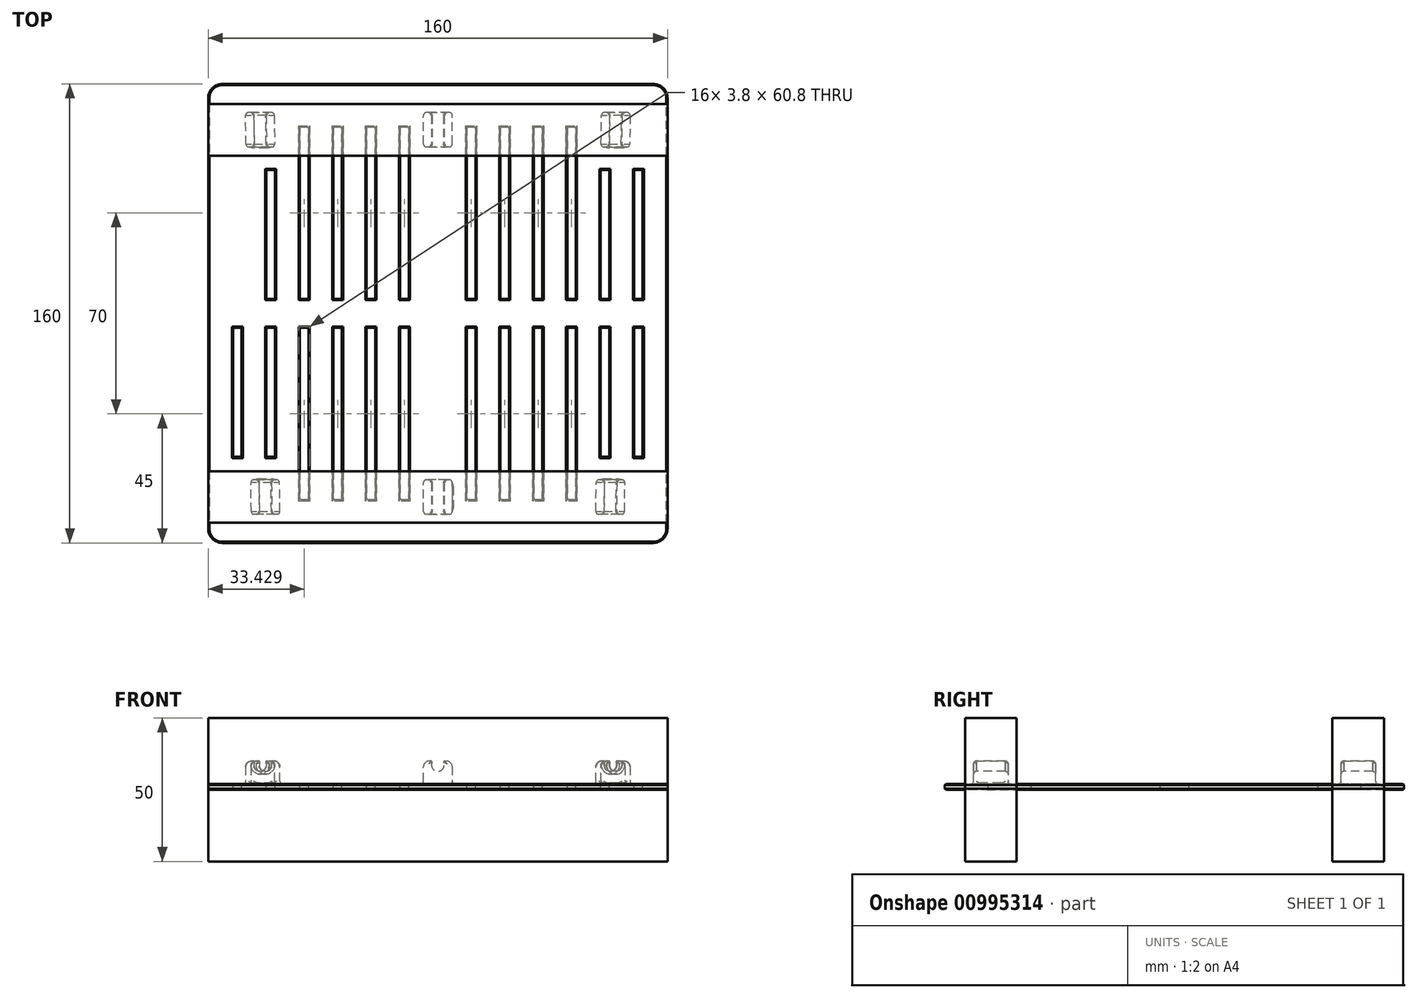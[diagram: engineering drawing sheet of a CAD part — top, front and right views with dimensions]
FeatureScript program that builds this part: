
annotation { "Feature Type Name" : "Feature", "Feature Type Description" : "" }
export const myFeature = defineFeature(function(context is Context, id is Id, definition is map)
    precondition{}
    {
        {
            var Q0;
            Q0=qCreatedBy(makeId("Front.planeOp"),FACE);
            cPlane(context, id + "F0", {"entities" : qUnion([Q0]), "cplaneType" : CPlaneType.OFFSET, "offset" : 70 * mm, "width" : 150 * mm, "height" : 150 * mm});
        }
        {
            var Q0;
            Q0=qCreatedBy(makeId("Front.planeOp"),FACE);
            cPlane(context, id + "F1", {"entities" : qUnion([Q0]), "cplaneType" : CPlaneType.OFFSET, "offset" : 70 * mm, "oppositeDirection" : true, "width" : 150 * mm, "height" : 150 * mm});
        }
        {
            var Q0;
            Q0=qCreatedBy(makeId("Top.planeOp"),FACE);
            cPlane(context, id + "F2", {"entities" : qUnion([Q0]), "cplaneType" : CPlaneType.OFFSET, "offset" : 25 * mm, "width" : 150 * mm, "height" : 150 * mm});
        }
        {
            var Q0;
            Q0=qCreatedBy(makeId("Top.planeOp"),FACE);
            var sketch = newSketch(context, id + "F3", { "sketchPlane" : qUnion([Q0])});
            skLineSegment(sketch, "E0.bottom", {"start": v(-75, 80) * mm, "end": v(75, 80) * mm});
            skLineSegment(sketch, "E0.top", {"start": v(-75, -80) * mm, "end": v(75, -80) * mm});
            skLineSegment(sketch, "E0.left", {"start": v(-80, 75) * mm, "end": v(-80, -75) * mm});
            skLineSegment(sketch, "E0.right", {"start": v(80, 75) * mm, "end": v(80, -75) * mm});
            skLineSegment(sketch, "E1", {"start": v(-80, 80) * mm, "end": v(80, -80) * mm, "construction": true});
            skPoint(sketch, "E2.visualSharp", {"position": v(-80, 80) * mm});
            skArc(sketch, "E2.filletArc", {"start": v(-75, 80) * mm, "mid": v(-78.54, 78.54) * mm, "end": v(-80, 75) * mm});
            skPoint(sketch, "E3.visualSharp", {"position": v(80, 80) * mm});
            skArc(sketch, "E3.filletArc", {"start": v(80, 75) * mm, "mid": v(78.54, 78.54) * mm, "end": v(75, 80) * mm});
            skPoint(sketch, "E4.visualSharp", {"position": v(80, -80) * mm});
            skArc(sketch, "E4.filletArc", {"start": v(75, -80) * mm, "mid": v(78.54, -78.54) * mm, "end": v(80, -75) * mm});
            skPoint(sketch, "E5.visualSharp", {"position": v(-80, -80) * mm});
            skArc(sketch, "E5.filletArc", {"start": v(-80, -75) * mm, "mid": v(-78.54, -78.54) * mm, "end": v(-75, -80) * mm});
            skSolve(sketch);
        }
        {
            var Q0;
            Q0 = qSketchRegion(id + "F3", true);
            extrude(context, id + "F4", {"entities" : qUnion([Q0]), "depth" : 2 * mm, "offsetDistance" : 25 * mm});
        }
        {
            var Q0;
            Q0=qCreatedBy(makeId("Right.planeOp"),FACE);
            var sketch = newSketch(context, id + "F5", { "sketchPlane" : qUnion([Q0])});
            skLineSegment(sketch, "E6.0", {"start": v(75, 2) * mm, "end": v(-75, 2) * mm, "construction": true});
            skLineSegment(sketch, "E7", {"start": v(0, 2) * mm, "end": v(0, -33.18) * mm, "construction": true});
            skLineSegment(sketch, "E8", {"start": v(0, 2) * mm, "end": v(58, 2) * mm});
            skLineSegment(sketch, "E9", {"start": v(58, 2) * mm, "end": v(58, 12) * mm});
            skLineSegment(sketch, "E10", {"start": v(58, 12) * mm, "end": v(-58, 12) * mm});
            skLineSegment(sketch, "E11", {"start": v(-58, 12) * mm, "end": v(-58, 2) * mm});
            skLineSegment(sketch, "E12", {"start": v(-58, 2) * mm, "end": v(0, 2) * mm});
            skSolve(sketch);
        }
        {
            var Q0;
            Q0=qCreatedBy(id+"F0.planeOp",FACE);
            var sketch = newSketch(context, id + "F6", { "sketchPlane" : qUnion([Q0])});
            skLineSegment(sketch, "E13.0", {"start": v(-75, 2) * mm, "end": v(75, 2) * mm, "construction": true});
            skLineSegment(sketch, "E14.bottom", {"start": v(55, 2) * mm, "end": v(65, 2) * mm});
            skLineSegment(sketch, "E14.top", {"start": v(55, 10) * mm, "end": v(65, 10) * mm, "construction": true});
            skLineSegment(sketch, "E14.left", {"start": v(55, 2) * mm, "end": v(55, 10) * mm});
            skLineSegment(sketch, "E14.right", {"start": v(65, 2) * mm, "end": v(65, 10) * mm});
            skLineSegment(sketch, "E15", {"start": v(0, 2) * mm, "end": v(0, 47.73) * mm, "construction": true});
            skArc(sketch, "E16", {"start": v(58.3, 10) * mm, "mid": v(60, 6.4) * mm, "end": v(61.7, 10) * mm});
            skLineSegment(sketch, "E17", {"start": v(60, 10) * mm, "end": v(60, 8.6) * mm, "construction": true});
            skLineSegment(sketch, "E18", {"start": v(55, 10) * mm, "end": v(58.3, 10) * mm});
            skLineSegment(sketch, "E19", {"start": v(65, 10) * mm, "end": v(61.7, 10) * mm});
            skLineSegment(sketch, "E20.MirrorCS", {"start": v(-55, 10) * mm, "end": v(-65, 10) * mm, "construction": true});
            skLineSegment(sketch, "E21.MirrorCS", {"start": v(-60, 10) * mm, "end": v(-60, 8.6) * mm, "construction": true});
            skLineSegment(sketch, "E22.MirrorCS", {"start": v(-55, 10) * mm, "end": v(-58.3, 10) * mm});
            skLineSegment(sketch, "E23.MirrorCS", {"start": v(-65, 10) * mm, "end": v(-61.7, 10) * mm});
            skLineSegment(sketch, "E24.MirrorCS", {"start": v(-55, 2) * mm, "end": v(-65, 2) * mm});
            skLineSegment(sketch, "E25.MirrorCS", {"start": v(-55, 2) * mm, "end": v(-55, 10) * mm});
            skLineSegment(sketch, "E26.MirrorCS", {"start": v(-65, 2) * mm, "end": v(-65, 10) * mm});
            skArc(sketch, "E27.MirrorCS", {"start": v(-58.3, 10) * mm, "mid": v(-60, 6.4) * mm, "end": v(-61.7, 10) * mm});
            skLineSegment(sketch, "E28", {"start": v(30, 2) * mm, "end": v(30, 33.9) * mm, "construction": true});
            skLineSegment(sketch, "E29", {"start": v(60, 8.6) * mm, "end": v(30, 8.6) * mm, "construction": true});
            skLineSegment(sketch, "E30", {"start": v(30, 8.6) * mm, "end": v(0, 8.6) * mm, "construction": true});
            skLineSegment(sketch, "E31.MirrorCS", {"start": v(-5, 10) * mm, "end": v(-1.7, 10) * mm});
            skLineSegment(sketch, "E32.MirrorCS", {"start": v(5, 10) * mm, "end": v(1.7, 10) * mm});
            skLineSegment(sketch, "E33.MirrorCS", {"start": v(-5, 2) * mm, "end": v(-5, 10) * mm});
            skLineSegment(sketch, "E34.MirrorCS", {"start": v(5, 10) * mm, "end": v(-5, 10) * mm, "construction": true});
            skLineSegment(sketch, "E35.MirrorCS", {"start": v(0, 10) * mm, "end": v(0, 8.6) * mm, "construction": true});
            skLineSegment(sketch, "E36.MirrorCS", {"start": v(5, 2) * mm, "end": v(-5, 2) * mm});
            skLineSegment(sketch, "E37.MirrorCS", {"start": v(5, 2) * mm, "end": v(5, 10) * mm});
            skArc(sketch, "E38.MirrorCS", {"start": v(1.7, 10) * mm, "mid": v(0, 6.4) * mm, "end": v(-1.7, 10) * mm});
            skSolve(sketch);
        }
        {
            var Q0;
            Q0=qCreatedBy(id+"F1.planeOp",FACE);
            var sketch = newSketch(context, id + "F7", { "sketchPlane" : qUnion([Q0])});
            skLineSegment(sketch, "E39.bottom", {"start": v(57, 2) * mm, "end": v(67, 2) * mm});
            skLineSegment(sketch, "E39.top", {"start": v(57, 10) * mm, "end": v(67, 10) * mm, "construction": true});
            skLineSegment(sketch, "E39.left", {"start": v(57, 2) * mm, "end": v(57, 10) * mm});
            skLineSegment(sketch, "E39.right", {"start": v(67, 2) * mm, "end": v(67, 10) * mm});
            skArc(sketch, "E40", {"start": v(60.3, 10) * mm, "mid": v(62, 6.4) * mm, "end": v(63.7, 10) * mm});
            skLineSegment(sketch, "E41", {"start": v(62, 10) * mm, "end": v(62, 8.6) * mm, "construction": true});
            skLineSegment(sketch, "E42", {"start": v(57, 10) * mm, "end": v(60.3, 10) * mm});
            skLineSegment(sketch, "E43", {"start": v(67, 10) * mm, "end": v(63.7, 10) * mm});
            skLineSegment(sketch, "E44.0", {"start": v(-75, 2) * mm, "end": v(75, 2) * mm, "construction": true});
            skLineSegment(sketch, "E45", {"start": v(0, 2) * mm, "end": v(0, 63.92) * mm, "construction": true});
            skPoint(sketch, "E45.endSnap0", {"position": v(0, 2) * mm});
            skLineSegment(sketch, "E46.MirrorCS", {"start": v(-67, 10) * mm, "end": v(-63.7, 10) * mm});
            skLineSegment(sketch, "E47.MirrorCS", {"start": v(-57, 10) * mm, "end": v(-60.3, 10) * mm});
            skLineSegment(sketch, "E48.MirrorCS", {"start": v(-57, 10) * mm, "end": v(-67, 10) * mm, "construction": true});
            skLineSegment(sketch, "E49.MirrorCS", {"start": v(-62, 10) * mm, "end": v(-62, 8.6) * mm, "construction": true});
            skLineSegment(sketch, "E50.MirrorCS", {"start": v(-67, 2) * mm, "end": v(-67, 10) * mm});
            skLineSegment(sketch, "E51.MirrorCS", {"start": v(-57, 2) * mm, "end": v(-67, 2) * mm});
            skArc(sketch, "E52.MirrorCS", {"start": v(-60.3, 10) * mm, "mid": v(-62, 6.4) * mm, "end": v(-63.7, 10) * mm});
            skLineSegment(sketch, "E53.MirrorCS", {"start": v(-57, 2) * mm, "end": v(-57, 10) * mm});
            skLineSegment(sketch, "E54", {"start": v(31, 2) * mm, "end": v(31, 36.18) * mm, "construction": true});
            skLineSegment(sketch, "E55", {"start": v(62, 8.6) * mm, "end": v(31, 8.6) * mm, "construction": true});
            skLineSegment(sketch, "E56", {"start": v(31, 8.6) * mm, "end": v(0, 8.6) * mm, "construction": true});
            skLineSegment(sketch, "E57.MirrorCS", {"start": v(5, 10) * mm, "end": v(1.7, 10) * mm});
            skLineSegment(sketch, "E58.MirrorCS", {"start": v(5, 10) * mm, "end": v(-5, 10) * mm, "construction": true});
            skLineSegment(sketch, "E59.MirrorCS", {"start": v(0, 10) * mm, "end": v(0, 8.6) * mm, "construction": true});
            skLineSegment(sketch, "E60.MirrorCS", {"start": v(-5, 10) * mm, "end": v(-1.7, 10) * mm});
            skArc(sketch, "E61.MirrorCS", {"start": v(1.7, 10) * mm, "mid": v(0, 6.4) * mm, "end": v(-1.7, 10) * mm});
            skLineSegment(sketch, "E62.MirrorCS", {"start": v(5, 2) * mm, "end": v(5, 10) * mm});
            skLineSegment(sketch, "E63.MirrorCS", {"start": v(5, 2) * mm, "end": v(-5, 2) * mm});
            skLineSegment(sketch, "E64.MirrorCS", {"start": v(-5, 2) * mm, "end": v(-5, 10) * mm});
            skSolve(sketch);
        }
        {
            var Q1;
            Q1=makeQuery(id+"F6.imprint","IMPRINT",FACE,{"disambiguationData":[TD([[makeQuery(id+"F6.imprint","IMPRINT",EDGE,{"derivedFrom":sQuery(id+"F6.wireOp",EDGE,"E14.bottom")}),1.0]])]});
            var Q2;
            Q2=makeQuery(id+"F7.imprint","IMPRINT",FACE,{"disambiguationData":[TD([[makeQuery(id+"F7.imprint","IMPRINT",EDGE,{"derivedFrom":sQuery(id+"F7.wireOp",EDGE,"E39.bottom")}),1.0]])]});
            loft(context, id + "F8", {"operationType" : NewBodyOperationType.ADD, "sheetProfilesArray" : [{ "sheetProfileEntities" : qUnion([Q1]) }, { "sheetProfileEntities" : qUnion([Q2]) }]});
        }
        {
            var Q1;
            Q1=makeQuery(id+"F6.imprint","IMPRINT",FACE,{"disambiguationData":[TD([[makeQuery(id+"F6.imprint","IMPRINT",EDGE,{"derivedFrom":sQuery(id+"F6.wireOp",EDGE,"E22.MirrorCS")}),1.0]])]});
            var Q2;
            Q2=makeQuery(id+"F7.imprint","IMPRINT",FACE,{"disambiguationData":[TD([[makeQuery(id+"F7.imprint","IMPRINT",EDGE,{"derivedFrom":sQuery(id+"F7.wireOp",EDGE,"E47.MirrorCS")}),1.0]])]});
            loft(context, id + "F9", {"operationType" : NewBodyOperationType.ADD, "sheetProfilesArray" : [{ "sheetProfileEntities" : qUnion([Q1]) }, { "sheetProfileEntities" : qUnion([Q2]) }]});
        }
        {
            var Q1;
            Q1=makeQuery(id+"F6.imprint","IMPRINT",FACE,{"disambiguationData":[TD([[makeQuery(id+"F6.imprint","IMPRINT",EDGE,{"derivedFrom":sQuery(id+"F6.wireOp",EDGE,"E31.MirrorCS")}),-1.0]])]});
            var Q2;
            Q2=makeQuery(id+"F7.imprint","IMPRINT",FACE,{"disambiguationData":[TD([[makeQuery(id+"F7.imprint","IMPRINT",EDGE,{"derivedFrom":sQuery(id+"F7.wireOp",EDGE,"E57.MirrorCS")}),1.0]])]});
            loft(context, id + "F10", {"operationType" : NewBodyOperationType.ADD, "sheetProfilesArray" : [{ "sheetProfileEntities" : qUnion([Q1]) }, { "sheetProfileEntities" : qUnion([Q2]) }]});
        }
        {
            var Q0;
            Q0 = qSketchRegion(id + "F5", true);
            extrude(context, id + "F11", {"entities" : qUnion([Q0]), "operationType" : NewBodyOperationType.REMOVE, "endBound" : BoundingType.SYMMETRIC, "depth" : 140 * mm, "offsetDistance" : 25 * mm});
        }
        {
            var Q0;
            Q0=makeQuery(id+"F8.opLoft","SWEPT_EDGE",EDGE,{"disambiguationData":[OSD([sQuery(id+"F6.wireOp",EDGE,"E14.left"),sQuery(id+"F6.wireOp",EDGE,"E18"),sQuery(id+"F7.wireOp",EDGE,"E39.left"),sQuery(id+"F7.wireOp",EDGE,"E42")])]});
            var Q1;
            Q1=makeQuery(id+"F8.opLoft","SWEPT_EDGE",EDGE,{"disambiguationData":[OSD([sQuery(id+"F6.wireOp",EDGE,"E14.right"),sQuery(id+"F6.wireOp",EDGE,"E19"),sQuery(id+"F7.wireOp",EDGE,"E39.right"),sQuery(id+"F7.wireOp",EDGE,"E43")])]});
            var Q2;
            Q2=makeQuery(id+"F9.opLoft","SWEPT_EDGE",EDGE,{"disambiguationData":[OSD([sQuery(id+"F6.wireOp",EDGE,"E23.MirrorCS"),sQuery(id+"F6.wireOp",EDGE,"E26.MirrorCS"),sQuery(id+"F7.wireOp",EDGE,"E46.MirrorCS"),sQuery(id+"F7.wireOp",EDGE,"E50.MirrorCS")])]});
            var Q3;
            Q3=makeQuery(id+"F9.opLoft","SWEPT_EDGE",EDGE,{"disambiguationData":[OSD([sQuery(id+"F6.wireOp",EDGE,"E22.MirrorCS"),sQuery(id+"F6.wireOp",EDGE,"E25.MirrorCS"),sQuery(id+"F7.wireOp",EDGE,"E47.MirrorCS"),sQuery(id+"F7.wireOp",EDGE,"E53.MirrorCS")])]});
            var Q4;
            {var subQ0=sQuery(id+"F7.wireOp",EDGE,"E64.MirrorCS");var subQ1=sQuery(id+"F7.wireOp",EDGE,"E60.MirrorCS");var subQ3=sQuery(id+"F6.wireOp",EDGE,"E33.MirrorCS");var subQ4=sQuery(id+"F6.wireOp",EDGE,"E31.MirrorCS");Q4=makeQuery(id+"F11.boolean.opBoolean","SPLIT",EDGE,{"disambiguationData":[TD([makeQuery(id+"F11.opExtrude","SWEPT_FACE",FACE,{"disambiguationData":[OSD([sQuery(id+"F5.wireOp",EDGE,"E11")])]})])],"derivedFrom":makeQuery(id+"F10.opLoft","SWEPT_EDGE",EDGE,{"disambiguationData":[OSD([subQ4,subQ3,subQ1,subQ0])]})});}
            var Q5;
            {var subQ0=sQuery(id+"F7.wireOp",EDGE,"E62.MirrorCS");var subQ1=sQuery(id+"F7.wireOp",EDGE,"E57.MirrorCS");var subQ3=sQuery(id+"F6.wireOp",EDGE,"E37.MirrorCS");var subQ4=sQuery(id+"F6.wireOp",EDGE,"E32.MirrorCS");Q5=makeQuery(id+"F11.boolean.opBoolean","SPLIT",EDGE,{"disambiguationData":[TD([makeQuery(id+"F11.opExtrude","SWEPT_FACE",FACE,{"disambiguationData":[OSD([sQuery(id+"F5.wireOp",EDGE,"E11")])]})])],"derivedFrom":makeQuery(id+"F10.opLoft","SWEPT_EDGE",EDGE,{"disambiguationData":[OSD([subQ4,subQ3,subQ1,subQ0])]})});}
            var Q6;
            {var subQ0=sQuery(id+"F7.wireOp",EDGE,"E64.MirrorCS");var subQ2=sQuery(id+"F7.wireOp",EDGE,"E60.MirrorCS");var subQ3=sQuery(id+"F6.wireOp",EDGE,"E33.MirrorCS");var subQ4=sQuery(id+"F6.wireOp",EDGE,"E31.MirrorCS");Q6=makeQuery(id+"F11.boolean.opBoolean","SPLIT",EDGE,{"disambiguationData":[TD([makeQuery(id+"F11.opExtrude","SWEPT_FACE",FACE,{"disambiguationData":[OSD([sQuery(id+"F5.wireOp",EDGE,"E9")])]})])],"derivedFrom":makeQuery(id+"F10.opLoft","SWEPT_EDGE",EDGE,{"disambiguationData":[OSD([subQ4,subQ3,subQ2,subQ0])]})});}
            var Q7;
            {var subQ0=sQuery(id+"F7.wireOp",EDGE,"E62.MirrorCS");var subQ2=sQuery(id+"F7.wireOp",EDGE,"E57.MirrorCS");var subQ3=sQuery(id+"F6.wireOp",EDGE,"E37.MirrorCS");var subQ4=sQuery(id+"F6.wireOp",EDGE,"E32.MirrorCS");Q7=makeQuery(id+"F11.boolean.opBoolean","SPLIT",EDGE,{"disambiguationData":[TD([makeQuery(id+"F11.opExtrude","SWEPT_FACE",FACE,{"disambiguationData":[OSD([sQuery(id+"F5.wireOp",EDGE,"E9")])]})])],"derivedFrom":makeQuery(id+"F10.opLoft","SWEPT_EDGE",EDGE,{"disambiguationData":[OSD([subQ4,subQ3,subQ2,subQ0])]})});}
            fillet(context, id + "F12", {"entities" : qUnion([Q0, Q1, Q2, Q3, Q4, Q5, Q6, Q7]), "radius" : 2 * mm, "tangentPropagation" : true, "allowEdgeOverflow" : false});
        }
        {
            var Q0;
            Q0=makeQuery(id+"F9.opLoft","SWEPT_EDGE",EDGE,{"disambiguationData":[OSD([sQuery(id+"F6.wireOp",EDGE,"E23.MirrorCS"),sQuery(id+"F6.wireOp",EDGE,"E27.MirrorCS"),sQuery(id+"F7.wireOp",EDGE,"E46.MirrorCS"),sQuery(id+"F7.wireOp",EDGE,"E52.MirrorCS")])]});
            var Q1;
            Q1=makeQuery(id+"F9.opLoft","SWEPT_EDGE",EDGE,{"disambiguationData":[OSD([sQuery(id+"F6.wireOp",EDGE,"E22.MirrorCS"),sQuery(id+"F6.wireOp",EDGE,"E27.MirrorCS"),sQuery(id+"F7.wireOp",EDGE,"E47.MirrorCS"),sQuery(id+"F7.wireOp",EDGE,"E52.MirrorCS")])]});
            var Q2;
            Q2=makeQuery(id+"F8.opLoft","SWEPT_EDGE",EDGE,{"disambiguationData":[OSD([sQuery(id+"F6.wireOp",EDGE,"E16"),sQuery(id+"F6.wireOp",EDGE,"E18"),sQuery(id+"F7.wireOp",EDGE,"E40"),sQuery(id+"F7.wireOp",EDGE,"E42")])]});
            var Q3;
            Q3=makeQuery(id+"F8.opLoft","SWEPT_EDGE",EDGE,{"disambiguationData":[OSD([sQuery(id+"F6.wireOp",EDGE,"E16"),sQuery(id+"F6.wireOp",EDGE,"E19"),sQuery(id+"F7.wireOp",EDGE,"E40"),sQuery(id+"F7.wireOp",EDGE,"E43")])]});
            var Q4;
            {var subQ1=sQuery(id+"F7.wireOp",EDGE,"E61.MirrorCS");var subQ2=sQuery(id+"F7.wireOp",EDGE,"E60.MirrorCS");var subQ3=sQuery(id+"F6.wireOp",EDGE,"E38.MirrorCS");var subQ4=sQuery(id+"F6.wireOp",EDGE,"E31.MirrorCS");Q4=makeQuery(id+"F11.boolean.opBoolean","SPLIT",EDGE,{"disambiguationData":[TD([makeQuery(id+"F11.opExtrude","SWEPT_FACE",FACE,{"disambiguationData":[OSD([sQuery(id+"F5.wireOp",EDGE,"E9")])]})])],"derivedFrom":makeQuery(id+"F10.opLoft","SWEPT_EDGE",EDGE,{"disambiguationData":[OSD([subQ4,subQ3,subQ2,subQ1])]})});}
            var Q5;
            {var subQ0=sQuery(id+"F7.wireOp",EDGE,"E61.MirrorCS");var subQ2=sQuery(id+"F7.wireOp",EDGE,"E57.MirrorCS");var subQ3=sQuery(id+"F6.wireOp",EDGE,"E38.MirrorCS");var subQ4=sQuery(id+"F6.wireOp",EDGE,"E32.MirrorCS");Q5=makeQuery(id+"F11.boolean.opBoolean","SPLIT",EDGE,{"disambiguationData":[TD([makeQuery(id+"F11.opExtrude","SWEPT_FACE",FACE,{"disambiguationData":[OSD([sQuery(id+"F5.wireOp",EDGE,"E9")])]})])],"derivedFrom":makeQuery(id+"F10.opLoft","SWEPT_EDGE",EDGE,{"disambiguationData":[OSD([subQ4,subQ3,subQ2,subQ0])]})});}
            var Q6;
            {var subQ0=sQuery(id+"F7.wireOp",EDGE,"E61.MirrorCS");var subQ1=sQuery(id+"F7.wireOp",EDGE,"E60.MirrorCS");var subQ2=sQuery(id+"F6.wireOp",EDGE,"E38.MirrorCS");var subQ4=sQuery(id+"F6.wireOp",EDGE,"E31.MirrorCS");Q6=makeQuery(id+"F11.boolean.opBoolean","SPLIT",EDGE,{"disambiguationData":[TD([makeQuery(id+"F11.opExtrude","SWEPT_FACE",FACE,{"disambiguationData":[OSD([sQuery(id+"F5.wireOp",EDGE,"E11")])]})])],"derivedFrom":makeQuery(id+"F10.opLoft","SWEPT_EDGE",EDGE,{"disambiguationData":[OSD([subQ4,subQ2,subQ1,subQ0])]})});}
            var Q7;
            {var subQ0=sQuery(id+"F7.wireOp",EDGE,"E61.MirrorCS");var subQ1=sQuery(id+"F7.wireOp",EDGE,"E57.MirrorCS");var subQ2=sQuery(id+"F6.wireOp",EDGE,"E38.MirrorCS");var subQ3=sQuery(id+"F6.wireOp",EDGE,"E32.MirrorCS");Q7=makeQuery(id+"F11.boolean.opBoolean","SPLIT",EDGE,{"disambiguationData":[TD([makeQuery(id+"F11.opExtrude","SWEPT_FACE",FACE,{"disambiguationData":[OSD([sQuery(id+"F5.wireOp",EDGE,"E11")])]})])],"derivedFrom":makeQuery(id+"F10.opLoft","SWEPT_EDGE",EDGE,{"disambiguationData":[OSD([subQ3,subQ2,subQ1,subQ0])]})});}
            fillet(context, id + "F13", {"entities" : qUnion([Q0, Q1, Q2, Q3, Q4, Q5, Q6, Q7]), "radius" : .4 * mm, "tangentPropagation" : true, "allowEdgeOverflow" : false});
        }
        {
            var Q0;
            Q0=makeQuery(id+"F8.opLoft","SWEPT_FACE",FACE,{"disambiguationData":[OSD([sQuery(id+"F6.wireOp",EDGE,"E14.bottom"),sQuery(id+"F6.wireOp",EDGE,"E14.right"),sQuery(id+"F6.wireOp",EDGE,"E19"),sQuery(id+"F7.wireOp",EDGE,"E39.bottom"),sQuery(id+"F7.wireOp",EDGE,"E39.right"),sQuery(id+"F7.wireOp",EDGE,"E43")])]});
            var Q1;
            Q1=makeQuery(id+"F8.opLoft","SWEPT_FACE",FACE,{"disambiguationData":[OSD([sQuery(id+"F6.wireOp",EDGE,"E14.bottom"),sQuery(id+"F6.wireOp",EDGE,"E14.left"),sQuery(id+"F6.wireOp",EDGE,"E18"),sQuery(id+"F7.wireOp",EDGE,"E39.bottom"),sQuery(id+"F7.wireOp",EDGE,"E39.left"),sQuery(id+"F7.wireOp",EDGE,"E42")])]});
            var Q2;
            Q2=makeQuery(id+"F8.opLoft","CAP_FACE",FACE,{"disambiguationData":[OSD([makeQuery(id+"F6.imprint","IMPRINT",FACE,{"disambiguationData":[TD([[makeQuery(id+"F6.imprint","IMPRINT",EDGE,{"derivedFrom":sQuery(id+"F6.wireOp",EDGE,"E14.bottom")}),1.0]])]})])],"isStart":true});
            var Q3;
            Q3=makeQuery(id+"F8.opLoft","CAP_FACE",FACE,{"disambiguationData":[OSD([makeQuery(id+"F7.imprint","IMPRINT",FACE,{"disambiguationData":[TD([[makeQuery(id+"F7.imprint","IMPRINT",EDGE,{"derivedFrom":sQuery(id+"F7.wireOp",EDGE,"E39.bottom")}),1.0]])]})])],"isStart":true});
            var Q4;
            Q4=makeQuery(id+"F9.opLoft","SWEPT_FACE",FACE,{"disambiguationData":[OSD([sQuery(id+"F6.wireOp",EDGE,"E22.MirrorCS"),sQuery(id+"F6.wireOp",EDGE,"E24.MirrorCS"),sQuery(id+"F6.wireOp",EDGE,"E25.MirrorCS"),sQuery(id+"F7.wireOp",EDGE,"E47.MirrorCS"),sQuery(id+"F7.wireOp",EDGE,"E51.MirrorCS"),sQuery(id+"F7.wireOp",EDGE,"E53.MirrorCS")])]});
            var Q5;
            Q5=makeQuery(id+"F9.opLoft","CAP_FACE",FACE,{"disambiguationData":[OSD([makeQuery(id+"F6.imprint","IMPRINT",FACE,{"disambiguationData":[TD([[makeQuery(id+"F6.imprint","IMPRINT",EDGE,{"derivedFrom":sQuery(id+"F6.wireOp",EDGE,"E22.MirrorCS")}),1.0]])]})])],"isStart":true});
            var Q6;
            Q6=makeQuery(id+"F9.opLoft","SWEPT_FACE",FACE,{"disambiguationData":[OSD([sQuery(id+"F6.wireOp",EDGE,"E23.MirrorCS"),sQuery(id+"F6.wireOp",EDGE,"E24.MirrorCS"),sQuery(id+"F6.wireOp",EDGE,"E26.MirrorCS"),sQuery(id+"F7.wireOp",EDGE,"E46.MirrorCS"),sQuery(id+"F7.wireOp",EDGE,"E51.MirrorCS"),sQuery(id+"F7.wireOp",EDGE,"E50.MirrorCS")])]});
            var Q7;
            Q7=makeQuery(id+"F9.opLoft","CAP_FACE",FACE,{"disambiguationData":[OSD([makeQuery(id+"F7.imprint","IMPRINT",FACE,{"disambiguationData":[TD([[makeQuery(id+"F7.imprint","IMPRINT",EDGE,{"derivedFrom":sQuery(id+"F7.wireOp",EDGE,"E47.MirrorCS")}),1.0]])]})])],"isStart":true});
            var Q8;
            Q8=makeQuery(id+"F10.opLoft","CAP_FACE",FACE,{"disambiguationData":[OSD([makeQuery(id+"F6.imprint","IMPRINT",FACE,{"disambiguationData":[TD([[makeQuery(id+"F6.imprint","IMPRINT",EDGE,{"derivedFrom":sQuery(id+"F6.wireOp",EDGE,"E31.MirrorCS")}),-1.0]])]})])],"isStart":true});
            var Q9;
            {var subQ0=sQuery(id+"F7.wireOp",EDGE,"E61.MirrorCS");var subQ1=sQuery(id+"F7.wireOp",EDGE,"E60.MirrorCS");var subQ3=sQuery(id+"F6.wireOp",EDGE,"E38.MirrorCS");var subQ5=sQuery(id+"F6.wireOp",EDGE,"E31.MirrorCS");var subQ6=sQuery(id+"F7.wireOp",EDGE,"E64.MirrorCS");var subQ7=sQuery(id+"F6.wireOp",EDGE,"E33.MirrorCS");Q9=makeQuery(id+"F11.boolean.opBoolean","COPY",FACE,{"disambiguationData":[TD([makeQuery(id+"F10.opLoft","SWEPT_FACE",FACE,{"disambiguationData":[OSD([subQ5,subQ7,subQ3,subQ1,subQ0,subQ6])]})])],"derivedFrom":makeQuery(id+"F11.opExtrude","SWEPT_FACE",FACE,{"disambiguationData":[OSD([sQuery(id+"F5.wireOp",EDGE,"E9")])]})});}
            var Q10;
            {var subQ1=sQuery(id+"F7.wireOp",EDGE,"E60.MirrorCS");var subQ2=sQuery(id+"F7.wireOp",EDGE,"E63.MirrorCS");var subQ3=sQuery(id+"F7.wireOp",EDGE,"E64.MirrorCS");var subQ5=sQuery(id+"F6.wireOp",EDGE,"E33.MirrorCS");var subQ6=sQuery(id+"F6.wireOp",EDGE,"E31.MirrorCS");var subQ8=makeQuery(id+"F11.opExtrude","SWEPT_FACE",FACE,{"disambiguationData":[OSD([sQuery(id+"F5.wireOp",EDGE,"E9")])]});var subQ9=makeQuery(id+"F10.opLoft","SWEPT_FACE",FACE,{"disambiguationData":[OSD([subQ6,subQ5,sQuery(id+"F6.wireOp",EDGE,"E36.MirrorCS"),subQ1,subQ2,subQ3])]});Q10=makeQuery(id+"F12.opFillet","BLEND_EDGE",EDGE,{"blendedFrom":[makeQuery(id+"F11.boolean.opBoolean","SPLIT",EDGE,{"disambiguationData":[TD([subQ8])],"derivedFrom":makeQuery(id+"F10.opLoft","SWEPT_EDGE",EDGE,{"disambiguationData":[OSD([subQ6,subQ5,subQ1,subQ3])]})}),makeQuery(id+"F11.boolean.opBoolean","SPLIT",FACE,{"disambiguationData":[TD([subQ8])],"derivedFrom":subQ9})],"blendedInto":[makeQuery(id+"F11.boolean.opBoolean","SPLIT",FACE,{"disambiguationData":[TD([subQ8])],"derivedFrom":subQ9})]});}
            var Q11;
            {var subQ0=sQuery(id+"F7.wireOp",EDGE,"E64.MirrorCS");var subQ1=sQuery(id+"F7.wireOp",EDGE,"E60.MirrorCS");var subQ3=sQuery(id+"F6.wireOp",EDGE,"E33.MirrorCS");var subQ4=sQuery(id+"F6.wireOp",EDGE,"E31.MirrorCS");var subQ5=sQuery(id+"F6.wireOp",EDGE,"E36.MirrorCS");Q11=makeQuery(id+"F11.boolean.opBoolean","SPLIT",FACE,{"disambiguationData":[TD([makeQuery(id+"F11.opExtrude","SWEPT_FACE",FACE,{"disambiguationData":[OSD([sQuery(id+"F5.wireOp",EDGE,"E11")])]})])],"derivedFrom":makeQuery(id+"F10.opLoft","SWEPT_FACE",FACE,{"disambiguationData":[OSD([subQ4,subQ3,subQ5,subQ1,sQuery(id+"F7.wireOp",EDGE,"E63.MirrorCS"),subQ0])]})});}
            var Q12;
            {var subQ0=sQuery(id+"F7.wireOp",EDGE,"E61.MirrorCS");var subQ1=sQuery(id+"F7.wireOp",EDGE,"E60.MirrorCS");var subQ3=sQuery(id+"F6.wireOp",EDGE,"E38.MirrorCS");var subQ5=sQuery(id+"F6.wireOp",EDGE,"E31.MirrorCS");var subQ6=sQuery(id+"F7.wireOp",EDGE,"E64.MirrorCS");var subQ7=sQuery(id+"F6.wireOp",EDGE,"E33.MirrorCS");Q12=makeQuery(id+"F11.boolean.opBoolean","COPY",FACE,{"disambiguationData":[TD([makeQuery(id+"F10.opLoft","SWEPT_FACE",FACE,{"disambiguationData":[OSD([subQ5,subQ7,subQ3,subQ1,subQ0,subQ6])]})])],"derivedFrom":makeQuery(id+"F11.opExtrude","SWEPT_FACE",FACE,{"disambiguationData":[OSD([sQuery(id+"F5.wireOp",EDGE,"E11")])]})});}
            var Q13;
            Q13=makeQuery(id+"F10.opLoft","CAP_FACE",FACE,{"disambiguationData":[OSD([makeQuery(id+"F7.imprint","IMPRINT",FACE,{"disambiguationData":[TD([[makeQuery(id+"F7.imprint","IMPRINT",EDGE,{"derivedFrom":sQuery(id+"F7.wireOp",EDGE,"E57.MirrorCS")}),1.0]])]})])],"isStart":true});
            var Q14;
            {var subQ0=sQuery(id+"F7.wireOp",EDGE,"E62.MirrorCS");var subQ2=sQuery(id+"F7.wireOp",EDGE,"E57.MirrorCS");var subQ3=sQuery(id+"F7.wireOp",EDGE,"E63.MirrorCS");var subQ4=sQuery(id+"F6.wireOp",EDGE,"E37.MirrorCS");var subQ5=sQuery(id+"F6.wireOp",EDGE,"E32.MirrorCS");Q14=makeQuery(id+"F11.boolean.opBoolean","SPLIT",FACE,{"disambiguationData":[TD([makeQuery(id+"F11.opExtrude","SWEPT_FACE",FACE,{"disambiguationData":[OSD([sQuery(id+"F5.wireOp",EDGE,"E9")])]})])],"derivedFrom":makeQuery(id+"F10.opLoft","SWEPT_FACE",FACE,{"disambiguationData":[OSD([subQ5,sQuery(id+"F6.wireOp",EDGE,"E36.MirrorCS"),subQ4,subQ2,subQ0,subQ3])]})});}
            var Q15;
            {var subQ1=sQuery(id+"F7.wireOp",EDGE,"E60.MirrorCS");var subQ2=sQuery(id+"F7.wireOp",EDGE,"E63.MirrorCS");var subQ3=sQuery(id+"F7.wireOp",EDGE,"E64.MirrorCS");var subQ4=sQuery(id+"F6.wireOp",EDGE,"E33.MirrorCS");var subQ5=sQuery(id+"F6.wireOp",EDGE,"E31.MirrorCS");Q15=makeQuery(id+"F11.boolean.opBoolean","SPLIT",FACE,{"disambiguationData":[TD([makeQuery(id+"F11.opExtrude","SWEPT_FACE",FACE,{"disambiguationData":[OSD([sQuery(id+"F5.wireOp",EDGE,"E9")])]})])],"derivedFrom":makeQuery(id+"F10.opLoft","SWEPT_FACE",FACE,{"disambiguationData":[OSD([subQ5,subQ4,sQuery(id+"F6.wireOp",EDGE,"E36.MirrorCS"),subQ1,subQ2,subQ3])]})});}
            fillet(context, id + "F14", {"entities" : qUnion([Q0, Q1, Q2, Q3, Q4, Q5, Q6, Q7, Q8, Q9, Q10, Q11, Q12, Q13, Q14, Q15]), "radius" : 1 * mm, "tangentPropagation" : true, "allowEdgeOverflow" : false});
        }
        {
            var Q0;
            Q0=qCreatedBy(id+"F2.planeOp",FACE);
            var sketch = newSketch(context, id + "F15", { "sketchPlane" : qUnion([Q0])});
            skArc(sketch, "E65.0", {"start": v(-75, 80) * mm, "mid": v(-78.54, 78.54) * mm, "end": v(-80, 75) * mm, "construction": true});
            skLineSegment(sketch, "E66.0", {"start": v(-75, 80) * mm, "end": v(75, 80) * mm, "construction": true});
            skLineSegment(sketch, "E67.0", {"start": v(-80, 75) * mm, "end": v(-80, -75) * mm, "construction": true});
            skArc(sketch, "E68.0", {"start": v(-80, -75) * mm, "mid": v(-78.54, -78.54) * mm, "end": v(-75, -80) * mm, "construction": true});
            skLineSegment(sketch, "E69.0", {"start": v(-75, -80) * mm, "end": v(75, -80) * mm, "construction": true});
            skArc(sketch, "E70.0", {"start": v(75, -80) * mm, "mid": v(78.54, -78.54) * mm, "end": v(80, -75) * mm, "construction": true});
            skLineSegment(sketch, "E71.0", {"start": v(80, 75) * mm, "end": v(80, -75) * mm, "construction": true});
            skArc(sketch, "E72.0", {"start": v(80, 75) * mm, "mid": v(78.54, 78.54) * mm, "end": v(75, 80) * mm, "construction": true});
            skLineSegment(sketch, "E73.bottom", {"start": v(-80, 55) * mm, "end": v(80, 55) * mm});
            skLineSegment(sketch, "E73.top", {"start": v(-80, 73) * mm, "end": v(80, 73) * mm});
            skLineSegment(sketch, "E73.left", {"start": v(-80, 55) * mm, "end": v(-80, 73) * mm});
            skLineSegment(sketch, "E73.right", {"start": v(80, 55) * mm, "end": v(80, 73) * mm});
            skLineSegment(sketch, "E74.bottom", {"start": v(-80, -73) * mm, "end": v(80, -73) * mm});
            skLineSegment(sketch, "E74.top", {"start": v(-80, -55) * mm, "end": v(80, -55) * mm});
            skLineSegment(sketch, "E74.left", {"start": v(-80, -73) * mm, "end": v(-80, -55) * mm});
            skLineSegment(sketch, "E74.right", {"start": v(80, -73) * mm, "end": v(80, -55) * mm});
            skSolve(sketch);
        }
        {
            var Q0;
            Q0=makeQuery(id+"F11.boolean.opBoolean","MERGE",FACE,{"derivedFrom":[makeQuery(id+"F4.opExtrude","CAP_FACE",FACE,{"disambiguationData":[OSD([sQuery(id+"F3.wireOp",EDGE,"E0.bottom"),sQuery(id+"F3.wireOp",EDGE,"E0.top"),sQuery(id+"F3.wireOp",EDGE,"E0.left"),sQuery(id+"F3.wireOp",EDGE,"E0.right"),sQuery(id+"F3.wireOp",EDGE,"E2.filletArc"),sQuery(id+"F3.wireOp",EDGE,"E3.filletArc"),sQuery(id+"F3.wireOp",EDGE,"E4.filletArc"),sQuery(id+"F3.wireOp",EDGE,"E5.filletArc")])],"isStart":false})],"fromTools":[makeQuery(id+"F11.opExtrude","SWEPT_FACE",FACE,{"disambiguationData":[OSD([sQuery(id+"F5.wireOp",EDGE,"E8"),sQuery(id+"F5.wireOp",EDGE,"E12")])]})]});
            var sketch = newSketch(context, id + "F16", { "sketchPlane" : qUnion([Q0])});
            skLineSegment(sketch, "E75.0", {"start": v(-75, -80) * mm, "end": v(75, -80) * mm, "construction": true});
            skArc(sketch, "E75.1", {"start": v(75, -80) * mm, "mid": v(78.54, -78.54) * mm, "end": v(80, -75) * mm, "construction": true});
            skLineSegment(sketch, "E75.2", {"start": v(80, 75) * mm, "end": v(80, -75) * mm, "construction": true});
            skLineSegment(sketch, "E75.3", {"start": v(-80, 75) * mm, "end": v(-80, -75) * mm, "construction": true});
            skArc(sketch, "E75.4", {"start": v(-80, -75) * mm, "mid": v(-78.54, -78.54) * mm, "end": v(-75, -80) * mm, "construction": true});
            skArc(sketch, "E75.5", {"start": v(80, 75) * mm, "mid": v(78.54, 78.54) * mm, "end": v(75, 80) * mm, "construction": true});
            skLineSegment(sketch, "E75.6", {"start": v(-75, 80) * mm, "end": v(75, 80) * mm, "construction": true});
            skArc(sketch, "E75.7", {"start": v(-75, 80) * mm, "mid": v(-78.54, 78.54) * mm, "end": v(-80, 75) * mm, "construction": true});
            skLineSegment(sketch, "E76", {"start": v(-80, 0) * mm, "end": v(80, 0) * mm, "construction": true});
            skLineSegment(sketch, "E77", {"start": v(-80, 5) * mm, "end": v(80, 5) * mm, "construction": true});
            skLineSegment(sketch, "E78", {"start": v(-80, -5) * mm, "end": v(80, -5) * mm, "construction": true});
            skLineSegment(sketch, "E79", {"start": v(-80, 50) * mm, "end": v(80, 50) * mm, "construction": true});
            skLineSegment(sketch, "E80", {"start": v(-80, -50) * mm, "end": v(80, -50) * mm, "construction": true});
            skLineSegment(sketch, "E81", {"start": v(-80, 65) * mm, "end": v(80, 65) * mm, "construction": true});
            skLineSegment(sketch, "E82", {"start": v(-80, -65) * mm, "end": v(80, -65) * mm, "construction": true});
            skLineSegment(sketch, "E83", {"start": v(0, 65) * mm, "end": v(0, 50) * mm, "construction": true});
            skLineSegment(sketch, "E84", {"start": v(0, 50) * mm, "end": v(0, 5) * mm, "construction": true});
            skLineSegment(sketch, "E85", {"start": v(0, 5) * mm, "end": v(0, 0) * mm, "construction": true});
            skLineSegment(sketch, "E86", {"start": v(0, 0) * mm, "end": v(0, -5) * mm, "construction": true});
            skLineSegment(sketch, "E87", {"start": v(0, -5) * mm, "end": v(0, -50) * mm, "construction": true});
            skLineSegment(sketch, "E88", {"start": v(0, -50) * mm, "end": v(0, -65) * mm, "construction": true});
            skLineSegment(sketch, "E89.bottom", {"start": v(-71.36, -5) * mm, "end": v(-68.36, -5) * mm});
            skLineSegment(sketch, "E89.top", {"start": v(-71.36, -50) * mm, "end": v(-68.36, -50) * mm});
            skLineSegment(sketch, "E89.left", {"start": v(-71.36, -5) * mm, "end": v(-71.36, -50) * mm});
            skLineSegment(sketch, "E89.right", {"start": v(-68.36, -5) * mm, "end": v(-68.36, -50) * mm});
            skLineSegment(sketch, "E90.bottom", {"start": v(-59.71, -5) * mm, "end": v(-56.71, -5) * mm});
            skLineSegment(sketch, "E90.top", {"start": v(-59.71, -50) * mm, "end": v(-56.71, -50) * mm});
            skLineSegment(sketch, "E90.left", {"start": v(-59.71, -5) * mm, "end": v(-59.71, -50) * mm});
            skLineSegment(sketch, "E90.right", {"start": v(-56.71, -5) * mm, "end": v(-56.71, -50) * mm});
            skLineSegment(sketch, "E91", {"start": v(0, 65) * mm, "end": v(0, 80) * mm, "construction": true});
            skLineSegment(sketch, "E92", {"start": v(0, -65) * mm, "end": v(0, -80) * mm, "construction": true});
            skLineSegment(sketch, "E93", {"start": v(-80, -27.94) * mm, "end": v(-71.36, -27.94) * mm, "construction": true});
            skLineSegment(sketch, "E94", {"start": v(-71.36, -27.94) * mm, "end": v(-68.36, -27.94) * mm, "construction": true});
            skLineSegment(sketch, "E95", {"start": v(-68.36, -27.94) * mm, "end": v(-59.71, -27.94) * mm, "construction": true});
            skLineSegment(sketch, "E96", {"start": v(-59.71, -27.94) * mm, "end": v(-56.71, -27.94) * mm, "construction": true});
            skLineSegment(sketch, "E97.bottom", {"start": v(-48.07, -5) * mm, "end": v(-45.07, -5) * mm});
            skLineSegment(sketch, "E97.top", {"start": v(-48.07, -65) * mm, "end": v(-45.07, -65) * mm});
            skLineSegment(sketch, "E97.left", {"start": v(-48.07, -5) * mm, "end": v(-48.07, -65) * mm});
            skLineSegment(sketch, "E97.right", {"start": v(-45.07, -5) * mm, "end": v(-45.07, -65) * mm});
            skLineSegment(sketch, "E98.bottom", {"start": v(-36.43, -5) * mm, "end": v(-33.43, -5) * mm});
            skLineSegment(sketch, "E98.top", {"start": v(-36.43, -65) * mm, "end": v(-33.43, -65) * mm});
            skLineSegment(sketch, "E98.left", {"start": v(-36.43, -5) * mm, "end": v(-36.43, -65) * mm});
            skLineSegment(sketch, "E98.right", {"start": v(-33.43, -5) * mm, "end": v(-33.43, -65) * mm});
            skLineSegment(sketch, "E99.bottom", {"start": v(-24.79, -5) * mm, "end": v(-21.79, -5) * mm});
            skLineSegment(sketch, "E99.top", {"start": v(-24.79, -65) * mm, "end": v(-21.79, -65) * mm});
            skLineSegment(sketch, "E99.left", {"start": v(-24.79, -5) * mm, "end": v(-24.79, -65) * mm});
            skLineSegment(sketch, "E99.right", {"start": v(-21.79, -5) * mm, "end": v(-21.79, -65) * mm});
            skLineSegment(sketch, "E100", {"start": v(-56.71, -27.94) * mm, "end": v(-48.07, -27.94) * mm, "construction": true});
            skLineSegment(sketch, "E101", {"start": v(-48.07, -27.94) * mm, "end": v(-45.07, -27.94) * mm, "construction": true});
            skLineSegment(sketch, "E102", {"start": v(-45.07, -27.94) * mm, "end": v(-36.43, -27.94) * mm, "construction": true});
            skLineSegment(sketch, "E103", {"start": v(-36.43, -27.94) * mm, "end": v(-33.43, -27.94) * mm, "construction": true});
            skLineSegment(sketch, "E104", {"start": v(-33.43, -27.94) * mm, "end": v(-24.79, -27.94) * mm, "construction": true});
            skLineSegment(sketch, "E105", {"start": v(-24.79, -27.94) * mm, "end": v(-21.79, -27.94) * mm, "construction": true});
            skLineSegment(sketch, "E106.bottom", {"start": v(-13.14, -5) * mm, "end": v(-10.14, -5) * mm});
            skLineSegment(sketch, "E106.top", {"start": v(-13.14, -65) * mm, "end": v(-10.14, -65) * mm});
            skLineSegment(sketch, "E106.left", {"start": v(-13.14, -5) * mm, "end": v(-13.14, -65) * mm});
            skLineSegment(sketch, "E106.right", {"start": v(-10.14, -5) * mm, "end": v(-10.14, -65) * mm});
            skLineSegment(sketch, "E107", {"start": v(-21.79, -27.94) * mm, "end": v(-13.14, -27.94) * mm, "construction": true});
            skLineSegment(sketch, "E108", {"start": v(-13.14, -27.94) * mm, "end": v(-10.14, -27.94) * mm, "construction": true});
            skLineSegment(sketch, "E109.bottom", {"start": v(-1.5, -5) * mm, "end": v(1.5, -5) * mm});
            skLineSegment(sketch, "E109.top", {"start": v(-1.5, -50) * mm, "end": v(1.5, -50) * mm});
            skLineSegment(sketch, "E109.left", {"start": v(-1.5, -5) * mm, "end": v(-1.5, -50) * mm});
            skLineSegment(sketch, "E109.right", {"start": v(1.5, -5) * mm, "end": v(1.5, -50) * mm});
            skLineSegment(sketch, "E110", {"start": v(-1.5, -27.94) * mm, "end": v(1.5, -27.94) * mm, "construction": true});
            skLineSegment(sketch, "E111", {"start": v(-1.5, -31.6) * mm, "end": v(0, -31.6) * mm, "construction": true});
            skLineSegment(sketch, "E112", {"start": v(0, -31.6) * mm, "end": v(1.5, -31.6) * mm, "construction": true});
            skLineSegment(sketch, "E113", {"start": v(-10.14, -27.94) * mm, "end": v(-1.5, -27.94) * mm, "construction": true});
            skLineSegment(sketch, "E114.MirrorCS", {"start": v(71.36, -50) * mm, "end": v(68.36, -50) * mm});
            skLineSegment(sketch, "E115.MirrorCS", {"start": v(59.71, -50) * mm, "end": v(56.71, -50) * mm});
            skLineSegment(sketch, "E116.MirrorCS", {"start": v(59.71, -5) * mm, "end": v(56.71, -5) * mm});
            skLineSegment(sketch, "E117.MirrorCS", {"start": v(36.43, -5) * mm, "end": v(33.43, -5) * mm});
            skLineSegment(sketch, "E118.MirrorCS", {"start": v(48.07, -65) * mm, "end": v(45.07, -65) * mm});
            skLineSegment(sketch, "E119.MirrorCS", {"start": v(24.79, -5) * mm, "end": v(21.79, -5) * mm});
            skLineSegment(sketch, "E120.MirrorCS", {"start": v(13.14, -65) * mm, "end": v(10.14, -65) * mm});
            skLineSegment(sketch, "E121.MirrorCS", {"start": v(24.79, -65) * mm, "end": v(21.79, -65) * mm});
            skLineSegment(sketch, "E122.MirrorCS", {"start": v(71.36, -5) * mm, "end": v(68.36, -5) * mm});
            skLineSegment(sketch, "E123.MirrorCS", {"start": v(48.07, -5) * mm, "end": v(45.07, -5) * mm});
            skLineSegment(sketch, "E124.MirrorCS", {"start": v(13.14, -5) * mm, "end": v(10.14, -5) * mm});
            skLineSegment(sketch, "E125.MirrorCS", {"start": v(36.43, -65) * mm, "end": v(33.43, -65) * mm});
            skLineSegment(sketch, "E126.MirrorCS", {"start": v(36.43, -5) * mm, "end": v(36.43, -65) * mm});
            skLineSegment(sketch, "E127.MirrorCS", {"start": v(48.07, -5) * mm, "end": v(48.07, -65) * mm});
            skLineSegment(sketch, "E128.MirrorCS", {"start": v(56.71, -5) * mm, "end": v(56.71, -50) * mm});
            skLineSegment(sketch, "E129.MirrorCS", {"start": v(21.79, -5) * mm, "end": v(21.79, -65) * mm});
            skLineSegment(sketch, "E130.MirrorCS", {"start": v(68.36, -5) * mm, "end": v(68.36, -50) * mm});
            skLineSegment(sketch, "E131.MirrorCS", {"start": v(13.14, -5) * mm, "end": v(13.14, -65) * mm});
            skLineSegment(sketch, "E132.MirrorCS", {"start": v(71.36, -5) * mm, "end": v(71.36, -50) * mm});
            skLineSegment(sketch, "E133.MirrorCS", {"start": v(59.71, -5) * mm, "end": v(59.71, -50) * mm});
            skLineSegment(sketch, "E134.MirrorCS", {"start": v(45.07, -5) * mm, "end": v(45.07, -65) * mm});
            skLineSegment(sketch, "E135.MirrorCS", {"start": v(10.14, -5) * mm, "end": v(10.14, -65) * mm});
            skLineSegment(sketch, "E136.MirrorCS", {"start": v(33.43, -5) * mm, "end": v(33.43, -65) * mm});
            skLineSegment(sketch, "E137.MirrorCS", {"start": v(24.79, -5) * mm, "end": v(24.79, -65) * mm});
            skLineSegment(sketch, "E138.MirrorCS", {"start": v(1.5, -5) * mm, "end": v(-1.5, -5) * mm});
            skLineSegment(sketch, "E139.MirrorCS", {"start": v(1.5, -50) * mm, "end": v(-1.5, -50) * mm});
            skLineSegment(sketch, "E140.MirrorCS", {"start": v(71.36, -27.94) * mm, "end": v(68.36, -27.94) * mm, "construction": true});
            skLineSegment(sketch, "E141.MirrorCS", {"start": v(24.79, -27.94) * mm, "end": v(21.79, -27.94) * mm, "construction": true});
            skLineSegment(sketch, "E142.MirrorCS", {"start": v(13.14, -27.94) * mm, "end": v(10.14, -27.94) * mm, "construction": true});
            skLineSegment(sketch, "E143.MirrorCS", {"start": v(0, -31.6) * mm, "end": v(-1.5, -31.6) * mm, "construction": true});
            skLineSegment(sketch, "E144.MirrorCS", {"start": v(48.07, -27.94) * mm, "end": v(45.07, -27.94) * mm, "construction": true});
            skLineSegment(sketch, "E145.MirrorCS", {"start": v(59.71, -27.94) * mm, "end": v(56.71, -27.94) * mm, "construction": true});
            skLineSegment(sketch, "E146.MirrorCS", {"start": v(1.5, -31.6) * mm, "end": v(0, -31.6) * mm, "construction": true});
            skLineSegment(sketch, "E147.MirrorCS", {"start": v(36.43, -27.94) * mm, "end": v(33.43, -27.94) * mm, "construction": true});
            skLineSegment(sketch, "E148.MirrorCS", {"start": v(1.5, -27.94) * mm, "end": v(-1.5, -27.94) * mm, "construction": true});
            skLineSegment(sketch, "E149.MirrorCS", {"start": v(56.71, -27.94) * mm, "end": v(48.07, -27.94) * mm, "construction": true});
            skLineSegment(sketch, "E150.MirrorCS", {"start": v(33.43, -27.94) * mm, "end": v(24.79, -27.94) * mm, "construction": true});
            skLineSegment(sketch, "E151.MirrorCS", {"start": v(21.79, -27.94) * mm, "end": v(13.14, -27.94) * mm, "construction": true});
            skLineSegment(sketch, "E152.MirrorCS", {"start": v(10.14, -27.94) * mm, "end": v(1.5, -27.94) * mm, "construction": true});
            skLineSegment(sketch, "E153.MirrorCS", {"start": v(68.36, -27.94) * mm, "end": v(59.71, -27.94) * mm, "construction": true});
            skLineSegment(sketch, "E154.MirrorCS", {"start": v(45.07, -27.94) * mm, "end": v(36.43, -27.94) * mm, "construction": true});
            skLineSegment(sketch, "E155.MirrorCS", {"start": v(0, 50) * mm, "end": v(0, 65) * mm, "construction": true});
            skLineSegment(sketch, "E156.MirrorCS", {"start": v(-1.5, 27.94) * mm, "end": v(1.5, 27.94) * mm, "construction": true});
            skLineSegment(sketch, "E157.MirrorCS", {"start": v(1.5, 31.6) * mm, "end": v(0, 31.6) * mm, "construction": true});
            skLineSegment(sketch, "E158.MirrorCS", {"start": v(0, 31.6) * mm, "end": v(-1.5, 31.6) * mm, "construction": true});
            skLineSegment(sketch, "E159.MirrorCS", {"start": v(1.5, 50) * mm, "end": v(-1.5, 50) * mm});
            skLineSegment(sketch, "E160.MirrorCS", {"start": v(-1.5, 50) * mm, "end": v(1.5, 50) * mm});
            skLineSegment(sketch, "E161.MirrorCS", {"start": v(36.43, 5) * mm, "end": v(33.43, 5) * mm});
            skLineSegment(sketch, "E162.MirrorCS", {"start": v(24.79, 65) * mm, "end": v(21.79, 65) * mm});
            skLineSegment(sketch, "E163.MirrorCS", {"start": v(0, 31.6) * mm, "end": v(1.5, 31.6) * mm, "construction": true});
            skLineSegment(sketch, "E164.MirrorCS", {"start": v(24.79, 5) * mm, "end": v(21.79, 5) * mm});
            skLineSegment(sketch, "E165.MirrorCS", {"start": v(-13.14, 65) * mm, "end": v(-10.14, 65) * mm});
            skLineSegment(sketch, "E166.MirrorCS", {"start": v(48.07, 5) * mm, "end": v(45.07, 5) * mm});
            skLineSegment(sketch, "E167.MirrorCS", {"start": v(-24.79, 5) * mm, "end": v(-21.79, 5) * mm});
            skLineSegment(sketch, "E168.MirrorCS", {"start": v(48.07, 65) * mm, "end": v(45.07, 65) * mm});
            skLineSegment(sketch, "E169.MirrorCS", {"start": v(59.71, 5) * mm, "end": v(56.71, 5) * mm});
            skLineSegment(sketch, "E170.MirrorCS", {"start": v(13.14, 65) * mm, "end": v(10.14, 65) * mm});
            skLineSegment(sketch, "E171.MirrorCS", {"start": v(-71.36, 5) * mm, "end": v(-68.36, 5) * mm});
            skLineSegment(sketch, "E172.MirrorCS", {"start": v(71.36, 5) * mm, "end": v(68.36, 5) * mm});
            skLineSegment(sketch, "E173.MirrorCS", {"start": v(-36.43, 65) * mm, "end": v(-33.43, 65) * mm});
            skLineSegment(sketch, "E174.MirrorCS", {"start": v(-59.71, 50) * mm, "end": v(-56.71, 50) * mm});
            skLineSegment(sketch, "E175.MirrorCS", {"start": v(59.71, 50) * mm, "end": v(56.71, 50) * mm});
            skLineSegment(sketch, "E176.MirrorCS", {"start": v(-36.43, 5) * mm, "end": v(-33.43, 5) * mm});
            skLineSegment(sketch, "E177.MirrorCS", {"start": v(-24.79, 65) * mm, "end": v(-21.79, 65) * mm});
            skLineSegment(sketch, "E178.MirrorCS", {"start": v(-1.5, 31.6) * mm, "end": v(0, 31.6) * mm, "construction": true});
            skLineSegment(sketch, "E179.MirrorCS", {"start": v(-59.71, 5) * mm, "end": v(-56.71, 5) * mm});
            skLineSegment(sketch, "E180.MirrorCS", {"start": v(-71.36, 50) * mm, "end": v(-68.36, 50) * mm});
            skLineSegment(sketch, "E181.MirrorCS", {"start": v(-48.07, 5) * mm, "end": v(-45.07, 5) * mm});
            skLineSegment(sketch, "E182.MirrorCS", {"start": v(1.5, 5) * mm, "end": v(-1.5, 5) * mm});
            skLineSegment(sketch, "E183.MirrorCS", {"start": v(-48.07, 65) * mm, "end": v(-45.07, 65) * mm});
            skLineSegment(sketch, "E184.MirrorCS", {"start": v(-13.14, 5) * mm, "end": v(-10.14, 5) * mm});
            skLineSegment(sketch, "E185.MirrorCS", {"start": v(71.36, 50) * mm, "end": v(68.36, 50) * mm});
            skLineSegment(sketch, "E186.MirrorCS", {"start": v(13.14, 5) * mm, "end": v(10.14, 5) * mm});
            skLineSegment(sketch, "E187.MirrorCS", {"start": v(36.43, 65) * mm, "end": v(33.43, 65) * mm});
            skLineSegment(sketch, "E188.MirrorCS", {"start": v(-1.5, 5) * mm, "end": v(1.5, 5) * mm});
            skLineSegment(sketch, "E189.MirrorCS", {"start": v(1.5, 27.94) * mm, "end": v(-1.5, 27.94) * mm, "construction": true});
            skLineSegment(sketch, "E190.MirrorCS", {"start": v(-10.14, 5) * mm, "end": v(-10.14, 65) * mm});
            skLineSegment(sketch, "E191.MirrorCS", {"start": v(-56.71, 5) * mm, "end": v(-56.71, 50) * mm});
            skLineSegment(sketch, "E192.MirrorCS", {"start": v(-45.07, 5) * mm, "end": v(-45.07, 65) * mm});
            skLineSegment(sketch, "E193.MirrorCS", {"start": v(68.36, 5) * mm, "end": v(68.36, 50) * mm});
            skLineSegment(sketch, "E194.MirrorCS", {"start": v(36.43, 5) * mm, "end": v(36.43, 65) * mm});
            skLineSegment(sketch, "E195.MirrorCS", {"start": v(10.14, 5) * mm, "end": v(10.14, 65) * mm});
            skLineSegment(sketch, "E196.MirrorCS", {"start": v(45.07, 5) * mm, "end": v(45.07, 65) * mm});
            skLineSegment(sketch, "E197.MirrorCS", {"start": v(-13.14, 5) * mm, "end": v(-13.14, 65) * mm});
            skLineSegment(sketch, "E198.MirrorCS", {"start": v(-1.5, 5) * mm, "end": v(-1.5, 50) * mm});
            skLineSegment(sketch, "E199.MirrorCS", {"start": v(33.43, 5) * mm, "end": v(33.43, 65) * mm});
            skLineSegment(sketch, "E200.MirrorCS", {"start": v(1.5, 5) * mm, "end": v(1.5, 50) * mm});
            skLineSegment(sketch, "E201.MirrorCS", {"start": v(-48.07, 5) * mm, "end": v(-48.07, 65) * mm});
            skLineSegment(sketch, "E202.MirrorCS", {"start": v(-21.79, 5) * mm, "end": v(-21.79, 65) * mm});
            skLineSegment(sketch, "E203.MirrorCS", {"start": v(-36.43, 5) * mm, "end": v(-36.43, 65) * mm});
            skLineSegment(sketch, "E204.MirrorCS", {"start": v(-71.36, 5) * mm, "end": v(-71.36, 50) * mm});
            skLineSegment(sketch, "E205.MirrorCS", {"start": v(13.14, 5) * mm, "end": v(13.14, 65) * mm});
            skLineSegment(sketch, "E206.MirrorCS", {"start": v(-24.79, 5) * mm, "end": v(-24.79, 65) * mm});
            skLineSegment(sketch, "E207.MirrorCS", {"start": v(71.36, 5) * mm, "end": v(71.36, 50) * mm});
            skLineSegment(sketch, "E208.MirrorCS", {"start": v(59.71, 5) * mm, "end": v(59.71, 50) * mm});
            skLineSegment(sketch, "E209.MirrorCS", {"start": v(48.07, 5) * mm, "end": v(48.07, 65) * mm});
            skLineSegment(sketch, "E210.MirrorCS", {"start": v(-59.71, 5) * mm, "end": v(-59.71, 50) * mm});
            skLineSegment(sketch, "E211.MirrorCS", {"start": v(56.71, 5) * mm, "end": v(56.71, 50) * mm});
            skLineSegment(sketch, "E212.MirrorCS", {"start": v(-33.43, 5) * mm, "end": v(-33.43, 65) * mm});
            skLineSegment(sketch, "E213.MirrorCS", {"start": v(24.79, 5) * mm, "end": v(24.79, 65) * mm});
            skLineSegment(sketch, "E214.MirrorCS", {"start": v(21.79, 5) * mm, "end": v(21.79, 65) * mm});
            skLineSegment(sketch, "E215.MirrorCS", {"start": v(-68.36, 5) * mm, "end": v(-68.36, 50) * mm});
            skSolve(sketch);
        }
        {
            var Q0;
            Q0=makeQuery(id+"F16.imprint","IMPRINT",FACE,{"disambiguationData":[TD([[makeQuery(id+"F16.imprint","IMPRINT",EDGE,{"derivedFrom":sQuery(id+"F16.wireOp",EDGE,"E174.MirrorCS")}),-1.0]])]});
            var Q1;
            Q1=makeQuery(id+"F16.imprint","IMPRINT",FACE,{"disambiguationData":[TD([[makeQuery(id+"F16.imprint","IMPRINT",EDGE,{"derivedFrom":sQuery(id+"F16.wireOp",EDGE,"E89.bottom")}),-1.0]])]});
            var Q2;
            Q2=makeQuery(id+"F16.imprint","IMPRINT",FACE,{"disambiguationData":[TD([[makeQuery(id+"F16.imprint","IMPRINT",EDGE,{"derivedFrom":sQuery(id+"F16.wireOp",EDGE,"E90.bottom")}),-1.0]])]});
            var Q3;
            Q3=makeQuery(id+"F16.imprint","IMPRINT",FACE,{"disambiguationData":[TD([[makeQuery(id+"F16.imprint","IMPRINT",EDGE,{"derivedFrom":sQuery(id+"F16.wireOp",EDGE,"E180.MirrorCS")}),-1.0]])]});
            var Q4;
            Q4=makeQuery(id+"F16.imprint","IMPRINT",FACE,{"disambiguationData":[TD([[makeQuery(id+"F16.imprint","IMPRINT",EDGE,{"derivedFrom":sQuery(id+"F16.wireOp",EDGE,"E106.top")}),1.0]])]});
            var Q5;
            Q5=makeQuery(id+"F16.imprint","IMPRINT",FACE,{"disambiguationData":[TD([[makeQuery(id+"F16.imprint","IMPRINT",EDGE,{"derivedFrom":sQuery(id+"F16.wireOp",EDGE,"E177.MirrorCS")}),-1.0]])]});
            var Q6;
            Q6=makeQuery(id+"F16.imprint","IMPRINT",FACE,{"disambiguationData":[TD([[makeQuery(id+"F16.imprint","IMPRINT",EDGE,{"derivedFrom":sQuery(id+"F16.wireOp",EDGE,"E98.bottom")}),-1.0]])]});
            var Q7;
            Q7=makeQuery(id+"F16.imprint","IMPRINT",FACE,{"disambiguationData":[TD([[makeQuery(id+"F16.imprint","IMPRINT",EDGE,{"derivedFrom":sQuery(id+"F16.wireOp",EDGE,"E97.top")}),1.0]])]});
            var Q8;
            Q8=makeQuery(id+"F16.imprint","IMPRINT",FACE,{"disambiguationData":[TD([[makeQuery(id+"F16.imprint","IMPRINT",EDGE,{"derivedFrom":sQuery(id+"F16.wireOp",EDGE,"E99.bottom")}),-1.0]])]});
            var Q9;
            Q9=makeQuery(id+"F16.imprint","IMPRINT",FACE,{"disambiguationData":[TD([[makeQuery(id+"F16.imprint","IMPRINT",EDGE,{"derivedFrom":sQuery(id+"F16.wireOp",EDGE,"E173.MirrorCS")}),-1.0]])]});
            var Q10;
            Q10=makeQuery(id+"F16.imprint","IMPRINT",FACE,{"disambiguationData":[TD([[makeQuery(id+"F16.imprint","IMPRINT",EDGE,{"derivedFrom":sQuery(id+"F16.wireOp",EDGE,"E165.MirrorCS")}),-1.0]])]});
            var Q11;
            Q11=makeQuery(id+"F16.imprint","IMPRINT",FACE,{"disambiguationData":[TD([[makeQuery(id+"F16.imprint","IMPRINT",EDGE,{"derivedFrom":sQuery(id+"F16.wireOp",EDGE,"E181.MirrorCS")}),1.0]])]});
            var Q12;
            Q12=makeQuery(id+"F16.imprint","IMPRINT",FACE,{"disambiguationData":[TD([[makeQuery(id+"F16.imprint","IMPRINT",EDGE,{"derivedFrom":sQuery(id+"F16.wireOp",EDGE,"E119.MirrorCS")}),1.0]])]});
            var Q13;
            Q13=makeQuery(id+"F16.imprint","IMPRINT",FACE,{"disambiguationData":[TD([[makeQuery(id+"F16.imprint","IMPRINT",EDGE,{"derivedFrom":sQuery(id+"F16.wireOp",EDGE,"E120.MirrorCS")}),-1.0]])]});
            var Q14;
            Q14=makeQuery(id+"F16.imprint","IMPRINT",FACE,{"disambiguationData":[TD([[makeQuery(id+"F16.imprint","IMPRINT",EDGE,{"derivedFrom":sQuery(id+"F16.wireOp",EDGE,"E125.MirrorCS")}),-1.0]])]});
            var Q15;
            Q15=makeQuery(id+"F16.imprint","IMPRINT",FACE,{"disambiguationData":[TD([[makeQuery(id+"F16.imprint","IMPRINT",EDGE,{"derivedFrom":sQuery(id+"F16.wireOp",EDGE,"E166.MirrorCS")}),-1.0]])]});
            var Q16;
            Q16=makeQuery(id+"F16.imprint","IMPRINT",FACE,{"disambiguationData":[TD([[makeQuery(id+"F16.imprint","IMPRINT",EDGE,{"derivedFrom":sQuery(id+"F16.wireOp",EDGE,"E118.MirrorCS")}),-1.0]])]});
            var Q17;
            Q17=makeQuery(id+"F16.imprint","IMPRINT",FACE,{"disambiguationData":[TD([[makeQuery(id+"F16.imprint","IMPRINT",EDGE,{"derivedFrom":sQuery(id+"F16.wireOp",EDGE,"E161.MirrorCS")}),-1.0]])]});
            var Q18;
            Q18=makeQuery(id+"F16.imprint","IMPRINT",FACE,{"disambiguationData":[TD([[makeQuery(id+"F16.imprint","IMPRINT",EDGE,{"derivedFrom":sQuery(id+"F16.wireOp",EDGE,"E164.MirrorCS")}),-1.0]])]});
            var Q19;
            Q19=makeQuery(id+"F16.imprint","IMPRINT",FACE,{"disambiguationData":[TD([[makeQuery(id+"F16.imprint","IMPRINT",EDGE,{"derivedFrom":sQuery(id+"F16.wireOp",EDGE,"E186.MirrorCS")}),-1.0]])]});
            var Q20;
            Q20=makeQuery(id+"F16.imprint","IMPRINT",FACE,{"disambiguationData":[TD([[makeQuery(id+"F16.imprint","IMPRINT",EDGE,{"derivedFrom":sQuery(id+"F16.wireOp",EDGE,"E115.MirrorCS")}),-1.0]])]});
            var Q21;
            Q21=makeQuery(id+"F16.imprint","IMPRINT",FACE,{"disambiguationData":[TD([[makeQuery(id+"F16.imprint","IMPRINT",EDGE,{"derivedFrom":sQuery(id+"F16.wireOp",EDGE,"E172.MirrorCS")}),-1.0]])]});
            var Q22;
            Q22=makeQuery(id+"F16.imprint","IMPRINT",FACE,{"disambiguationData":[TD([[makeQuery(id+"F16.imprint","IMPRINT",EDGE,{"derivedFrom":sQuery(id+"F16.wireOp",EDGE,"E122.MirrorCS")}),1.0]])]});
            var Q23;
            Q23=makeQuery(id+"F16.imprint","IMPRINT",FACE,{"disambiguationData":[TD([[makeQuery(id+"F16.imprint","IMPRINT",EDGE,{"derivedFrom":sQuery(id+"F16.wireOp",EDGE,"E169.MirrorCS")}),-1.0]])]});
            var Q24;
            Q24=makeQuery(id+"F16.imprint","IMPRINT",FACE,{"disambiguationData":[TD([[makeQuery(id+"F16.imprint","IMPRINT",EDGE,{"derivedFrom":sQuery(id+"F16.wireOp",EDGE,"E138.MirrorCS")}),1.0]])]});
            var Q25;
            Q25=makeQuery(id+"F16.imprint","IMPRINT",FACE,{"disambiguationData":[TD([[makeQuery(id+"F16.imprint","IMPRINT",EDGE,{"derivedFrom":sQuery(id+"F16.wireOp",EDGE,"E160.MirrorCS")}),-1.0]])]});
            extrude(context, id + "F17", {"entities" : qUnion([Q0, Q1, Q2, Q3, Q4, Q5, Q6, Q7, Q8, Q9, Q10, Q11, Q12, Q13, Q14, Q15, Q16, Q17, Q18, Q19, Q20, Q21, Q22, Q23, Q24, Q25]), "operationType" : NewBodyOperationType.REMOVE, "oppositeDirection" : true, "depth" : 25 * mm, "offsetDistance" : 25 * mm});
        }
        {
            var Q0;
            Q0=makeQuery(id+"F4.opExtrude","SWEPT_FACE",FACE,{"disambiguationData":[OSD([sQuery(id+"F3.wireOp",EDGE,"E0.left")])]});
            var Q1;
            Q1=makeQuery(id+"F4.opExtrude","SWEPT_FACE",FACE,{"disambiguationData":[OSD([sQuery(id+"F3.wireOp",EDGE,"E2.filletArc")])]});
            var Q2;
            Q2=makeQuery(id+"F4.opExtrude","SWEPT_FACE",FACE,{"disambiguationData":[OSD([sQuery(id+"F3.wireOp",EDGE,"E0.bottom")])]});
            var Q3;
            Q3=makeQuery(id+"F4.opExtrude","SWEPT_FACE",FACE,{"disambiguationData":[OSD([sQuery(id+"F3.wireOp",EDGE,"E5.filletArc")])]});
            var Q4;
            Q4=makeQuery(id+"F4.opExtrude","SWEPT_FACE",FACE,{"disambiguationData":[OSD([sQuery(id+"F3.wireOp",EDGE,"E0.top")])]});
            var Q5;
            Q5=makeQuery(id+"F4.opExtrude","SWEPT_FACE",FACE,{"disambiguationData":[OSD([sQuery(id+"F3.wireOp",EDGE,"E4.filletArc")])]});
            var Q6;
            Q6=makeQuery(id+"F4.opExtrude","SWEPT_FACE",FACE,{"disambiguationData":[OSD([sQuery(id+"F3.wireOp",EDGE,"E0.right")])]});
            var Q7;
            Q7=makeQuery(id+"F4.opExtrude","SWEPT_FACE",FACE,{"disambiguationData":[OSD([sQuery(id+"F3.wireOp",EDGE,"E3.filletArc")])]});
            var Q8;
            Q8=makeQuery(id+"F4.opExtrude","CAP_FACE",FACE,{"disambiguationData":[OSD([sQuery(id+"F3.wireOp",EDGE,"E0.bottom"),sQuery(id+"F3.wireOp",EDGE,"E0.top"),sQuery(id+"F3.wireOp",EDGE,"E0.left"),sQuery(id+"F3.wireOp",EDGE,"E0.right"),sQuery(id+"F3.wireOp",EDGE,"E2.filletArc"),sQuery(id+"F3.wireOp",EDGE,"E3.filletArc"),sQuery(id+"F3.wireOp",EDGE,"E4.filletArc"),sQuery(id+"F3.wireOp",EDGE,"E5.filletArc")])],"isStart":true});
            var Q9;
            Q9=makeQuery(id+"F11.boolean.opBoolean","MERGE",FACE,{"derivedFrom":[makeQuery(id+"F4.opExtrude","CAP_FACE",FACE,{"disambiguationData":[OSD([sQuery(id+"F3.wireOp",EDGE,"E0.bottom"),sQuery(id+"F3.wireOp",EDGE,"E0.top"),sQuery(id+"F3.wireOp",EDGE,"E0.left"),sQuery(id+"F3.wireOp",EDGE,"E0.right"),sQuery(id+"F3.wireOp",EDGE,"E2.filletArc"),sQuery(id+"F3.wireOp",EDGE,"E3.filletArc"),sQuery(id+"F3.wireOp",EDGE,"E4.filletArc"),sQuery(id+"F3.wireOp",EDGE,"E5.filletArc")])],"isStart":false})],"fromTools":[makeQuery(id+"F11.opExtrude","SWEPT_FACE",FACE,{"disambiguationData":[OSD([sQuery(id+"F5.wireOp",EDGE,"E8"),sQuery(id+"F5.wireOp",EDGE,"E12")])]})]});
            chamfer(context, id + "F18", {"entities" : qUnion([Q0, Q1, Q2, Q3, Q4, Q5, Q6, Q7, Q8, Q9]), "width" : .4 * mm, "tangentPropagation" : true});
        }
        {
            var Q0;
            Q0 = qSketchRegion(id + "F15", true);
            extrude(context, id + "F19", {"entities" : qUnion([Q0]), "oppositeDirection" : true, "depth" : 50 * mm, "offsetDistance" : 25 * mm});
        }
    });
